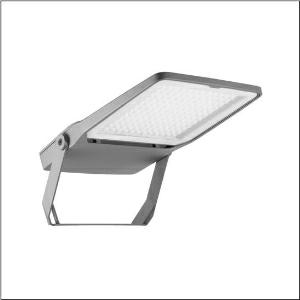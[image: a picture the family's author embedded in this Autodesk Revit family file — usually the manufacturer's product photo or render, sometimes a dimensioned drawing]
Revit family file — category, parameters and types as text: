
# Revit family: floodlight_fl_20_midi___pl61_5xa7682e2c1ac_2141
name_source: partatom
category: Lighting Fixtures
units: mm (PartAtom-declared; Revit-internal decimal feet)

## family parameters
Cut with Voids When Loaded = No
Host = Face
Light Source = No
Part Type = Normal
Room Calculation Point = No
Round Connector Dimension = Use Diameter
Shared = No

## types (1)
- --- (1 x LED 4000K / CRI = 70 (unbekannt), 27150 lm, 4000K)
    Apparent Load = 208 VA
    CIE Flux Codes = 33 65 98 100 100
    Color Rendering = 70
    Color Temperature = 4000K
    Default Elevation = 1800 mm
    Description = Floodlight FL 20 midi, floodlight, primary light control with lens, of plastic, primary optical cover: protective disc, of toughened safety glass, transparent, light distribution: PL61, light emission: direct distribution, primary light characteristic: asymmetric, installation type: surface-mounted, LED, High Power LED, rated luminous flux: 27.150lm, luminous efficacy: 131lm/W, light colour: 740, colour temperature: 4000K, control gear: ECG Plus, control: flexible luminous flux parameterisation, time-dependent luminous flux control, digital communication interface, power reduction, overheat protection, electronic power reduction, with terminal, 5-pole, max. 2.5mm², mains connection: 220..240V, AC, 50/60Hz, rated input power: 208W, LED unit, of diecast aluminium, powder-coated, Siteco® metallic grey (DB 702S), corrosivity category C5 mid according to DIN EN ISO 12944, incl. 1x M20 cable gland for cable Ø 6.5..12mm, length: 654mm, width: 450mm, height: 76mm, housing frame, of diecast aluminium, powder-coated, Siteco® metallic grey (DB 702S), mounting bracket, of steel, powder-coated, Siteco® metallic grey (DB 702S), DALI, protection rating (complete): IP66, insulation class (complete): insulation class II (safety insulation), certification: CE, ENEC, VDE, protection symbol: D, permissible operating ambient temperature: -40..+40°C, permissible operating ambient temperature for outdoor applications: -40..+50°C, standard: DIN EN 12944, packaging unit: 1 piece

Light Distribution: PL61
    Height = 76 mm
    Lamp = 1 x LED 4000K / CRI >= 70 (unbekannt)
    Lamp Light Flux = 27150 lm
    Lamp count = 1
    Length = 672 mm
    Luminous efficacy = 131 lm/W
    Manufacturer = Siteco
    ModVariant = No
    Model = 5XA7682E2C1AC
    Mounting Place = Wall
    Mounting Type = Surface mounted
    Number of Poles = 1
    OnlyDefault = Yes
    Power Factor = 1
    Product Name = Floodlight FL 20 midi | PL61
    Product group = floodlight | wall mounted
    ProductGroupID = 2001
    Protection Class = Protection class II
    Protection Degree = IP 66
    RLX_Detail_Level = 1
    RLX_Emergency_Light_Flux = 0 lm
    RLX_Emergency_Type = 0
    RLX_Emergency_Type_DB = No
    RlxData = <blob elided: 97953 chars, md5=3104ff8c>
    Socket = socket
    Standby Power = 0 W
    System Light Flux = 27150 lm
    System Power = 208 W
    Type Comments = factory setting: luminous flux: 100 % | dim-lin: 254 | 484 mA
    Type Image = l_1005943.jpg
    URL = http://relux.com
    VarID = @adj_146953
    Voltage = 0 V
    Weight = 0.00 kg
    Width = 450 mm

## geometry (parser evidence)
native form markers: Blend x4, Sweep x14
no freeform markers — native parametric forms only
